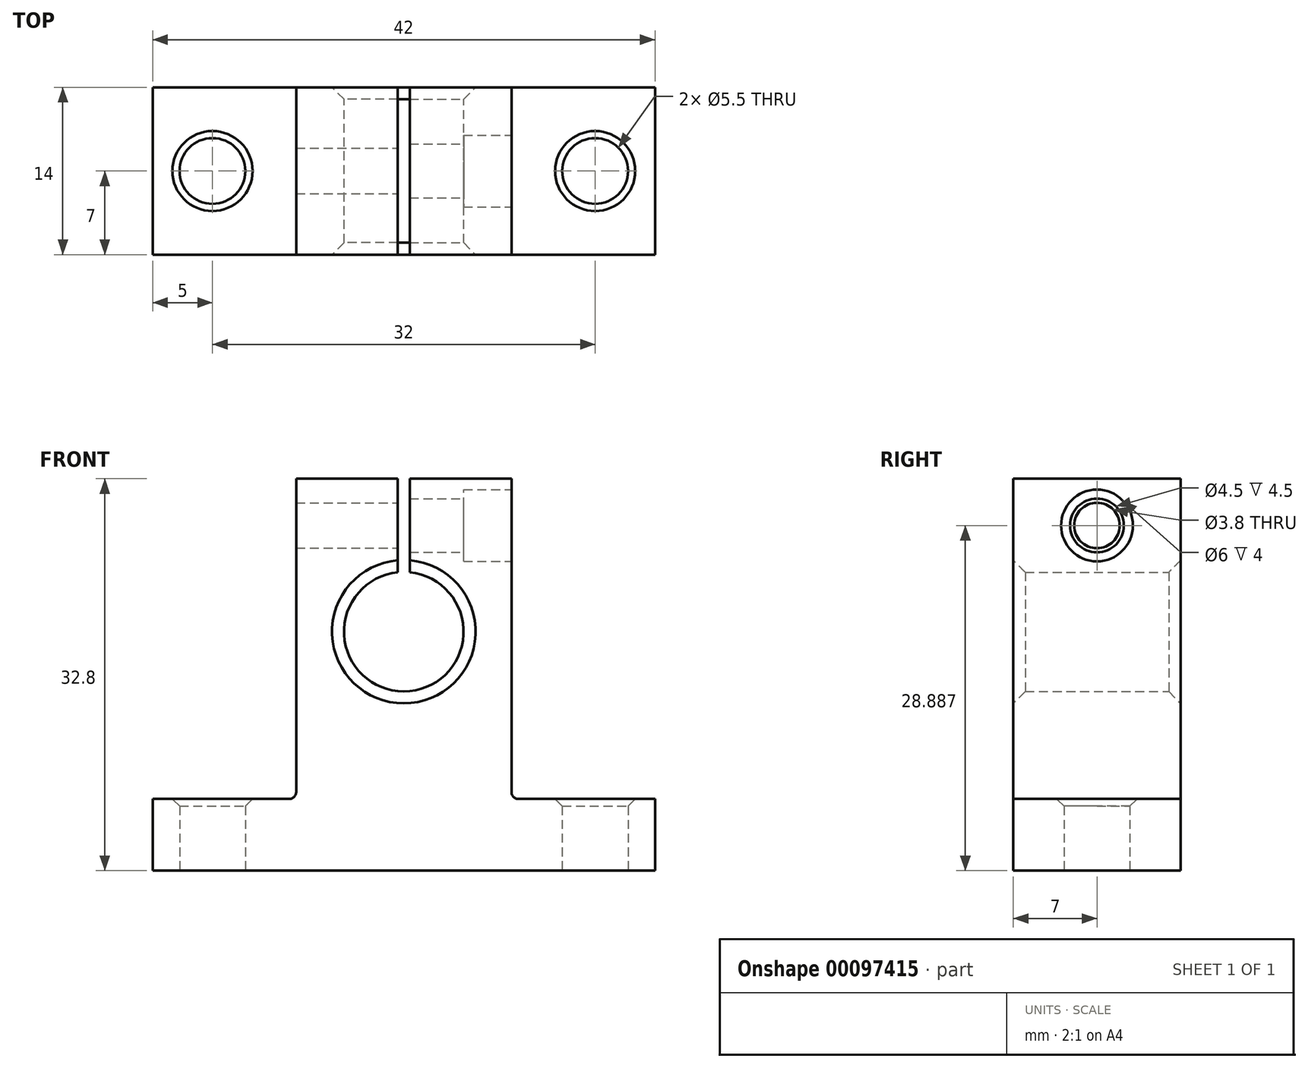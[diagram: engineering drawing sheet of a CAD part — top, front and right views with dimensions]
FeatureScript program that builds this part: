
annotation { "Feature Type Name" : "Feature", "Feature Type Description" : "" }
export const myFeature = defineFeature(function(context is Context, id is Id, definition is map)
    precondition{}
    {
        {
            var Q0;
            Q0=qCreatedBy(makeId("Front.planeOp"),FACE);
            var sketch = newSketch(context, id + "F0", { "sketchPlane" : qUnion([Q0])});
            skLineSegment(sketch, "E0", {"start": v(0, 0) * mm, "end": v(0, 814.55) * mm, "construction": true});
            skLineSegment(sketch, "E1", {"start": v(0, 0) * mm, "end": v(21, 0) * mm});
            skLineSegment(sketch, "E2", {"start": v(21, 0) * mm, "end": v(21, 6) * mm});
            skLineSegment(sketch, "E3", {"start": v(21, 6) * mm, "end": v(9, 6) * mm});
            skLineSegment(sketch, "E4", {"start": v(9, 6) * mm, "end": v(9, 32.8) * mm});
            skLineSegment(sketch, "E5", {"start": v(9, 32.8) * mm, "end": v(0.5, 32.8) * mm});
            skLineSegment(sketch, "E6.MirrorCS", {"start": v(0, 0) * mm, "end": v(-21, 0) * mm});
            skLineSegment(sketch, "E7.MirrorCS", {"start": v(-21, 0) * mm, "end": v(-21, 6) * mm});
            skLineSegment(sketch, "E8.MirrorCS", {"start": v(-21, 6) * mm, "end": v(-9, 6) * mm});
            skLineSegment(sketch, "E9.MirrorCS", {"start": v(-9, 32.8) * mm, "end": v(-0.5, 32.8) * mm});
            skLineSegment(sketch, "E10.MirrorCS", {"start": v(-9, 6) * mm, "end": v(-9, 32.8) * mm});
            skArc(sketch, "E11", {"start": v(-0.5, 24.97) * mm, "mid": v(0, 15) * mm, "end": v(0.5, 24.97) * mm});
            skLineSegment(sketch, "E12", {"start": v(0.5, 32.8) * mm, "end": v(0.5, 24.97) * mm});
            skLineSegment(sketch, "E13", {"start": v(-0.5, 32.8) * mm, "end": v(-0.5, 24.97) * mm});
            skPoint(sketch, "E14.orphan", {"position": v(0, 32.8) * mm});
            skSolve(sketch);
        }
        {
            var Q0;
            Q0 = qSketchRegion(id + "F0", true);
            extrude(context, id + "F1", {"entities" : qUnion([Q0]), "depth" : 14 * mm});
        }
        {
            var Q0;
            Q0=makeQuery(id+"F1.opExtrude","SWEPT_FACE",FACE,{"disambiguationData":[OSD([sQuery(id+"F0.wireOp",EDGE,"E1"),sQuery(id+"F0.wireOp",EDGE,"E6.MirrorCS")])]});
            var sketch = newSketch(context, id + "F2", { "sketchPlane" : qUnion([Q0])});
            skLineSegment(sketch, "E15", {"start": v(0, 0) * mm, "end": v(0, 20.04) * mm, "construction": true});
            skLineSegment(sketch, "E16", {"start": v(-21, 7) * mm, "end": v(21, 7) * mm, "construction": true});
            skCircle(sketch, "E17", {"center": v(-16, 7) * mm, "radius": 2.75 * mm});
            skCircle(sketch, "E18", {"center": v(16, 7) * mm, "radius": 2.75 * mm});
            skSolve(sketch);
        }
        {
            var Q0;
            Q0 = qSketchRegion(id + "F2", true);
            extrude(context, id + "F3", {"entities" : qUnion([Q0]), "operationType" : NewBodyOperationType.REMOVE, "endBound" : BoundingType.THROUGH_ALL, "oppositeDirection" : true, "depth" : 25 * mm});
        }
        {
            var Q0;
            Q0=makeQuery(id+"F1.opExtrude","CAP_EDGE",EDGE,{"disambiguationData":[OSD([sQuery(id+"F0.wireOp",EDGE,"E11")])],"isStart":false});
            var Q1;
            Q1=makeQuery(id+"F1.opExtrude","CAP_EDGE",EDGE,{"disambiguationData":[OSD([sQuery(id+"F0.wireOp",EDGE,"E11")])],"isStart":true});
            chamfer(context, id + "F4", {"entities" : qUnion([Q0, Q1]), "width" : 1 * mm, "tangentPropagation" : true});
        }
        {
            var Q0;
            Q0=makeQuery(id+"F1.opExtrude","SWEPT_EDGE",EDGE,{"disambiguationData":[OSD([sQuery(id+"F0.wireOp",EDGE,"E3"),sQuery(id+"F0.wireOp",EDGE,"E4")])]});
            var Q1;
            Q1=makeQuery(id+"F1.opExtrude","SWEPT_EDGE",EDGE,{"disambiguationData":[OSD([sQuery(id+"F0.wireOp",EDGE,"E8.MirrorCS"),sQuery(id+"F0.wireOp",EDGE,"E10.MirrorCS")])]});
            fillet(context, id + "F5", {"entities" : qUnion([Q0, Q1]), "radius" : 0.6 * mm, "tangentPropagation" : true, "allowEdgeOverflow" : false});
        }
        {
            var Q0;
            Q0=makeQuery(id+"F3.boolean.opBoolean","INTERSECT",EDGE,{"derivedFrom":[makeQuery(id+"F1.opExtrude","SWEPT_FACE",FACE,{"disambiguationData":[OSD([sQuery(id+"F0.wireOp",EDGE,"E3")])]}),makeQuery(id+"F3.opExtrude","SWEPT_FACE",FACE,{"disambiguationData":[OSD([sQuery(id+"F2.wireOp",EDGE,"E18")])]})]});
            var Q1;
            Q1=makeQuery(id+"F3.boolean.opBoolean","INTERSECT",EDGE,{"derivedFrom":[makeQuery(id+"F1.opExtrude","SWEPT_FACE",FACE,{"disambiguationData":[OSD([sQuery(id+"F0.wireOp",EDGE,"E8.MirrorCS")])]}),makeQuery(id+"F3.opExtrude","SWEPT_FACE",FACE,{"disambiguationData":[OSD([sQuery(id+"F2.wireOp",EDGE,"E17")])]})]});
            chamfer(context, id + "F6", {"entities" : qUnion([Q0, Q1]), "width" : 0.6 * mm, "tangentPropagation" : true});
        }
        {
            var Q0;
            Q0=makeQuery(id+"F1.opExtrude","SWEPT_FACE",FACE,{"disambiguationData":[OSD([sQuery(id+"F0.wireOp",EDGE,"E13")])]});
            var sketch = newSketch(context, id + "F7", { "sketchPlane" : qUnion([Q0])});
            skLineSegment(sketch, "E19", {"start": v(-7, 32.8) * mm, "end": v(-7, 24.97) * mm, "construction": true});
            skCircle(sketch, "E20", {"center": v(-7, 28.89) * mm, "radius": 1.9 * mm});
            skSolve(sketch);
        }
        {
            var Q0;
            Q0 = qSketchRegion(id + "F7", true);
            extrude(context, id + "F8", {"entities" : qUnion([Q0]), "operationType" : NewBodyOperationType.REMOVE, "endBound" : BoundingType.THROUGH_ALL, "oppositeDirection" : true, "depth" : 25 * mm, "hasSecondDirection" : true, "secondDirectionBound" : SecondDirectionBoundingType.THROUGH_ALL, "secondDirectionOppositeDirection" : false, "secondDirectionDepth" : 25 * mm});
        }
        {
            var Q0;
            Q0=makeQuery(id+"F1.opExtrude","SWEPT_FACE",FACE,{"disambiguationData":[OSD([sQuery(id+"F0.wireOp",EDGE,"E4")])]});
            var sketch = newSketch(context, id + "F9", { "sketchPlane" : qUnion([Q0])});
            skCircle(sketch, "E21", {"center": v(-7, 28.89) * mm, "radius": 2.25 * mm});
            skSolve(sketch);
        }
        {
            var Q0;
            Q0 = qSketchRegion(id + "F9", true);
            var Q1;
            Q1=makeQuery(id+"F1.opExtrude","SWEPT_FACE",FACE,{"disambiguationData":[OSD([sQuery(id+"F0.wireOp",EDGE,"E13")])]});
            extrude(context, id + "F10", {"entities" : qUnion([Q0]), "operationType" : NewBodyOperationType.REMOVE, "endBound" : BoundingType.UP_TO_SURFACE, "oppositeDirection" : true, "endBoundEntityFace" : qUnion([Q1]), "depth" : 25 * mm});
        }
        {
            var Q0;
            Q0=makeQuery(id+"F1.opExtrude","SWEPT_FACE",FACE,{"disambiguationData":[OSD([sQuery(id+"F0.wireOp",EDGE,"E4")])]});
            var sketch = newSketch(context, id + "F11", { "sketchPlane" : qUnion([Q0])});
            skCircle(sketch, "E22", {"center": v(-7, 28.89) * mm, "radius": 3 * mm});
            skSolve(sketch);
        }
        {
            var Q0;
            Q0 = qSketchRegion(id + "F11", true);
            extrude(context, id + "F12", {"entities" : qUnion([Q0]), "operationType" : NewBodyOperationType.REMOVE, "oppositeDirection" : true, "depth" : 4 * mm});
        }
    });
